# Revit family: P191568KX-091c_KVWB406D
name_source: partatom
category: Specialty Equipment
units: mm (PartAtom-declared; Revit-internal decimal feet)

## family parameters
Always vertical = Yes
Cut with Voids When Loaded = No
Enable Cutting in Views = No
Maintain Annotation Orientation = No
Part Type = Normal
Room Calculation Point = No
Round Connector Dimension = Use Diameter
Shared = No
Work Plane-Based = No

## types (1)
- KVWB406DSS
    Accent Material = ARCAT - Metal - Steel - Gray
    Amps = 15 A
    Body Material = ARCAT - Metal - Steel - Stainless
    Default Elevation = 0"
    Depth = 20"
    Description = 36'' Wall-Mount, 3-Speed Canopy Hood
Hotte aspirante murale à 3 vitesses de 36 po
    Dimension Guide = http://access.whirlpool.com Guide&sku=KVWB406DSS&language=EN
http://access.whirlpool.com Guide&sku=KVWB406DSS&language=EN
    Family Name = COOKING
    Feature 1 = 400 CFM/65K BTU Threshold
Seuil de 65 000 BTU, 400 pi cu/min.
    Feature 2 = Perimeter Ventilation
Ventilation périmétrique
    Feature 3 = LED Task Lights
Éclairage de surface de travail à DEL
    Height = 28 7/8"
    Installation-Fabrication = http://access.whirlpool.com Instruction&sku=KVWB406DSS&language=EN
http://access.whirlpool.com Instruction&sku=KVWB406DSS&language=FR
    Manufacturer = KitchenAid
    Model = KVWB406DSS
    Voltage = 0 V
    Width = 36"

## geometry (parser evidence)
native form markers: Sweep x5
no freeform markers — native parametric forms only
